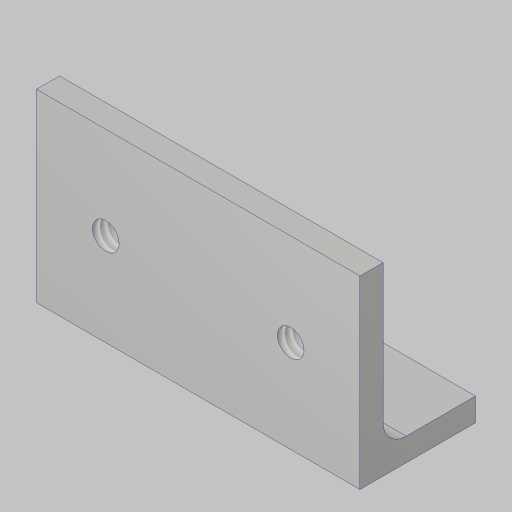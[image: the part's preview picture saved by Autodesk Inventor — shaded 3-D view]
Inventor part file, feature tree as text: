
AUTODESK INVENTOR PART (.ipt)
format: ipt  version: 2023.5 (Build 275446000, 446)  size: 130,048 bytes
history: native  units: in
note: dims shown in document units (in); Inventor stores cm internally (conversion verified against a paired STEP export)
features: sketch x3, hole x2, extrude x1, fillet x1
ambient origin geometry x8: Origin, YZ Plane, XZ Plane, XY Plane, X Axis, Y Axis, Z Axis, Center Point
bodies: Solid1 (feature_tree)
feature tree (7):
  extrude  "Extrusion1"  Depth=0.125in
  fillet  "Fillet1"  Radius=1.75in
  hole  "Hole1"  [1 undecoded]
  hole  "Hole2"  [1 undecoded]
  sketch  "Sketch1"  dims[d0=1.0in d2=0.125in d3=1.75in d4=0.0in]
  sketch  "Sketch2"  dims[d5=0.125in d6=0.25in]
  sketch  "Sketch3"  dims[d7=1.2598in d8=0.104in d9=0.276in d10=0.119in d11=0.25in d12=0.5635in d13=1.0in d14=0.8108in d15=1.0in d21=0.625in d22=0.5in d23=0.145in d24=0.38in d25=0.375in d26=0.25in d27=0.5635in d28=1.0in d29=0.8108in]
note: 2 required parameter values undecoded (feature->parameter linkage not recoverable at this tier; creation-order binding heuristic only, values carry confidence <= 0.55)
